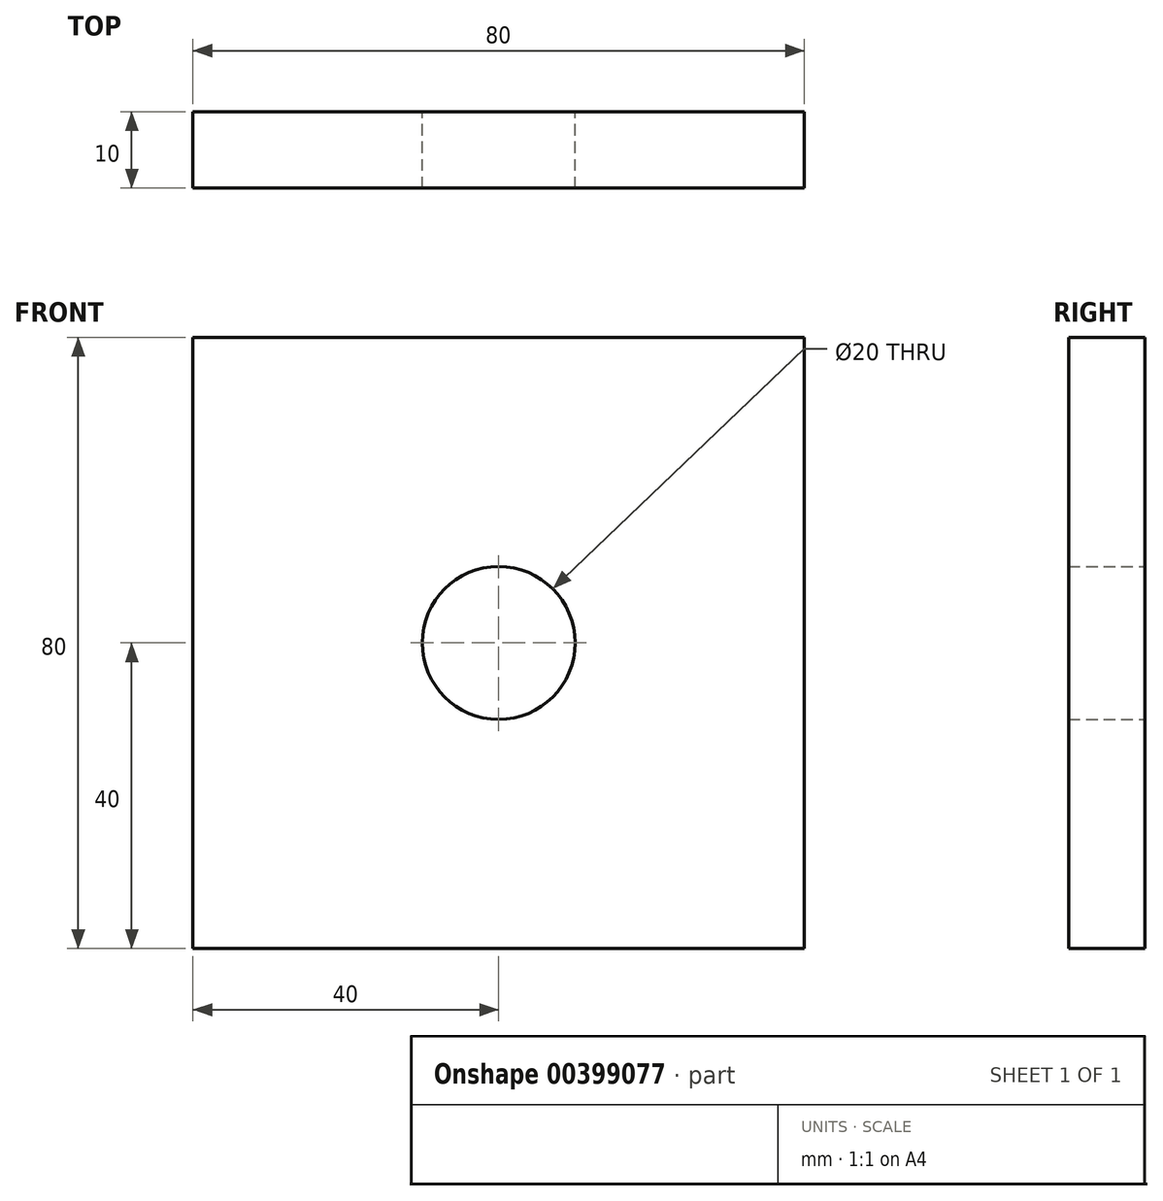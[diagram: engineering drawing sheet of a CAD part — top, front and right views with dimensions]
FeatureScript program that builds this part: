
annotation { "Feature Type Name" : "Feature", "Feature Type Description" : "" }
export const myFeature = defineFeature(function(context is Context, id is Id, definition is map)
    precondition{}
    {
        {
            var Q0;
            Q0=qCreatedBy(makeId("Front.planeOp"),FACE);
            var sketch = newSketch(context, id + "F0", { "sketchPlane" : qUnion([Q0])});
            skLineSegment(sketch, "E0.bottom", {"start": v(-40, 40) * mm, "end": v(40, 40) * mm});
            skLineSegment(sketch, "E0.top", {"start": v(-40, -40) * mm, "end": v(40, -40) * mm});
            skLineSegment(sketch, "E0.left", {"start": v(-40, 40) * mm, "end": v(-40, -40) * mm});
            skLineSegment(sketch, "E0.right", {"start": v(40, 40) * mm, "end": v(40, -40) * mm});
            skCircle(sketch, "E1", {"center": v(0, 0) * mm, "radius": 10 * mm});
            skSolve(sketch);
        }
        {
            var Q0;
            Q0=makeQuery(id+"F0.imprint","IMPRINT",FACE,{"disambiguationData":[TD([[makeQuery(id+"F0.imprint","IMPRINT",EDGE,{"derivedFrom":sQuery(id+"F0.wireOp",EDGE,"E0.bottom")}),-1.0]])]});
            extrude(context, id + "F1", {"entities" : qUnion([Q0]), "depth" : 10 * mm});
        }
    });
